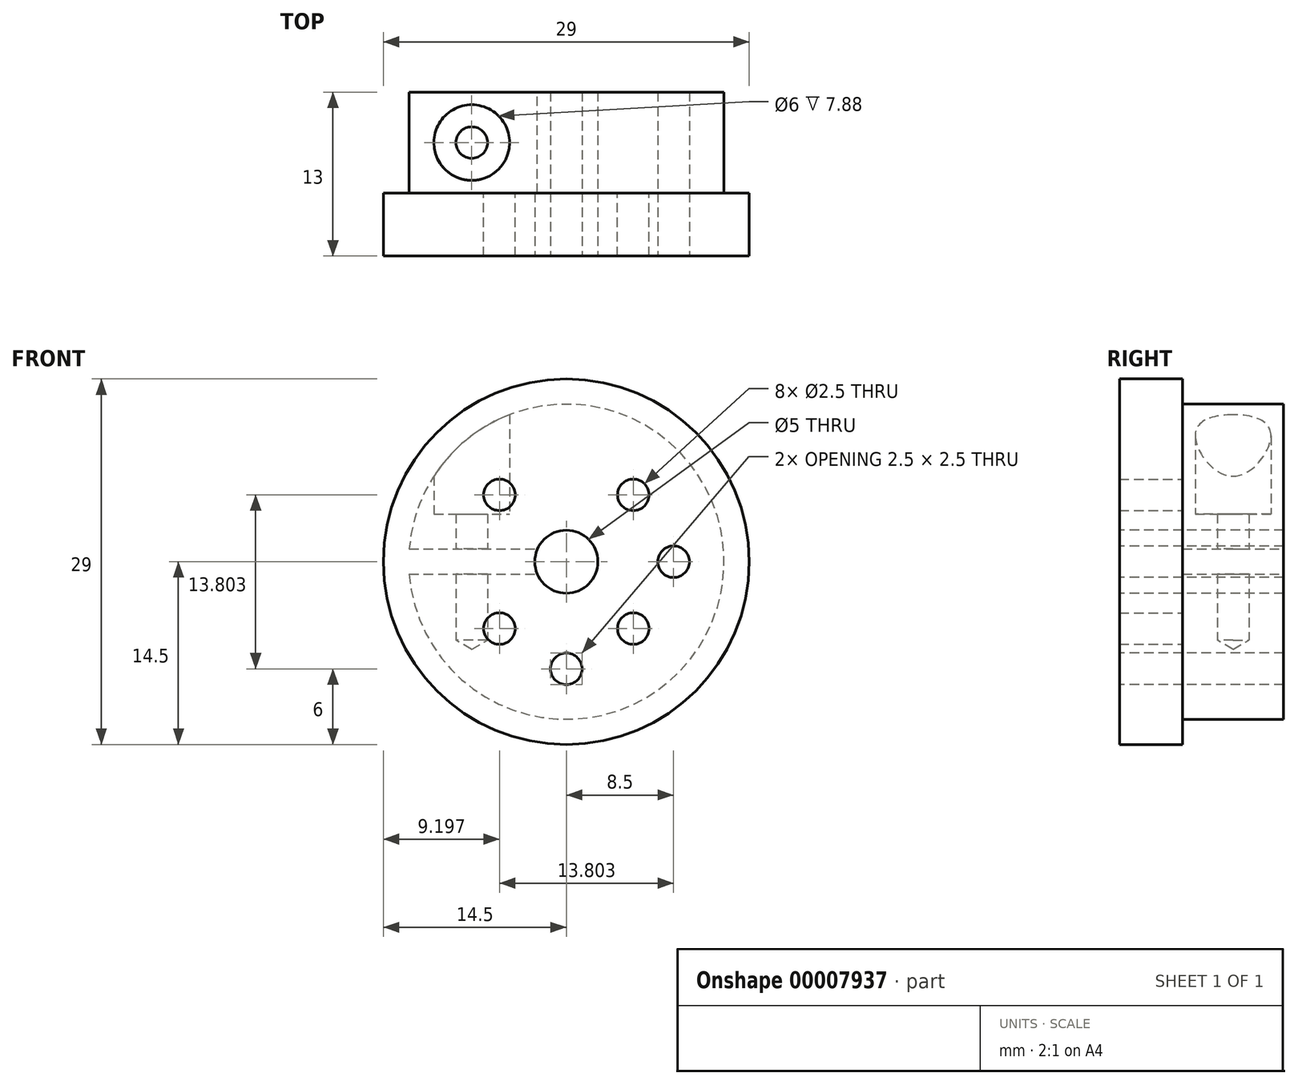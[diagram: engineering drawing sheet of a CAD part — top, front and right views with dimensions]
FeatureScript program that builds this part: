
annotation { "Feature Type Name" : "Feature", "Feature Type Description" : "" }
export const myFeature = defineFeature(function(context is Context, id is Id, definition is map)
    precondition{}
    {
        {
            var Q0;
            Q0=qCreatedBy(makeId("Right.planeOp"),FACE);
            var sketch = newSketch(context, id + "F0", { "sketchPlane" : qUnion([Q0])});
            skLineSegment(sketch, "E0.bottom", {"start": v(-4, 12.5) * mm, "end": v(4, 12.5) * mm});
            skLineSegment(sketch, "E0.top", {"start": v(-4, 2.5) * mm, "end": v(4, 2.5) * mm});
            skLineSegment(sketch, "E0.left", {"start": v(-4, 12.5) * mm, "end": v(-4, 2.5) * mm});
            skLineSegment(sketch, "E0.right", {"start": v(4, 12.5) * mm, "end": v(4, 2.5) * mm});
            skLineSegment(sketch, "E1", {"start": v(-8.98, 0) * mm, "end": v(8.74, 0) * mm, "construction": true});
            skLineSegment(sketch, "E2", {"start": v(0, 0) * mm, "end": v(0, 20.32) * mm, "construction": true});
            skPoint(sketch, "E3", {"position": v(0, 12.5) * mm});
            skLineSegment(sketch, "E4.bottom", {"start": v(-4, 2.5) * mm, "end": v(-9, 2.5) * mm});
            skLineSegment(sketch, "E4.top", {"start": v(-4, 14.5) * mm, "end": v(-9, 14.5) * mm});
            skLineSegment(sketch, "E4.left", {"start": v(-4, 2.5) * mm, "end": v(-4, 14.5) * mm});
            skLineSegment(sketch, "E4.right", {"start": v(-9, 2.5) * mm, "end": v(-9, 14.5) * mm});
            skSolve(sketch);
        }
        {
            var Q0;
            Q0=makeQuery(id+"F0.imprint","IMPRINT",FACE,{"disambiguationData":[TD([[makeQuery(id+"F0.imprint","IMPRINT",EDGE,{"derivedFrom":sQuery(id+"F0.wireOp",EDGE,"E0.bottom")}),-1.0]])]});
            var Q1;
            Q1=sQuery(id+"F0.wireOp",EDGE,"E1");
            revolve(context, id + "F1", {"entities" : qUnion([Q0]), "axis" : qUnion([Q1]), "revolveType" : RevolveType.FULL});
        }
        {
            var Q0;
            Q0=makeQuery(id+"F1.opRevolve","SWEPT_FACE",FACE,{"disambiguationData":[OSD([sQuery(id+"F0.wireOp",EDGE,"E0.right")])]});
            var sketch = newSketch(context, id + "F2", { "sketchPlane" : qUnion([Q0])});
            skPoint(sketch, "E5", {"position": v(-8.5, 0) * mm});
            skPoint(sketch, "E6.1.0", {"position": v(0, -8.5) * mm});
            skPoint(sketch, "E6.center", {"position": v(0, 0) * mm});
            skLineSegment(sketch, "E6.anchor1", {"start": v(0, 0) * mm, "end": v(-8.5, 0) * mm, "construction": true});
            skLineSegment(sketch, "E6.anchor2", {"start": v(0, 0) * mm, "end": v(0, -8.5) * mm, "construction": true});
            skLineSegment(sketch, "E7.bottom", {"start": v(12.73, 1) * mm, "end": v(2.1, 1) * mm});
            skLineSegment(sketch, "E7.top", {"start": v(12.73, -1) * mm, "end": v(2.1, -1) * mm});
            skLineSegment(sketch, "E7.left", {"start": v(12.73, 1) * mm, "end": v(12.73, -1) * mm});
            skLineSegment(sketch, "E7.right", {"start": v(2.1, 1) * mm, "end": v(2.1, -1) * mm});
            skPoint(sketch, "E7.middle", {"position": v(7.42, 0) * mm});
            skSolve(sketch);
        }
        {
            var Q0;
            {var subQ0=sQuery(id+"F2.wireOp",EDGE,"E7.bottom");var subQ1=sQuery(id+"F0.wireOp",EDGE,"E0.right");var subQ2=makeQuery(id+"F1.opRevolve","SWEPT_EDGE",EDGE,{"disambiguationData":[OSD([sQuery(id+"F0.wireOp",EDGE,"E0.bottom"),subQ1])]});var subQ3=makeQuery(id+"F2.imprint","INTERSECT",VERTEX,{"derivedFrom":[subQ2,subQ0]});Q0=makeQuery(id+"F2.imprint","IMPRINT",FACE,{"disambiguationData":[TD([[makeQuery(id+"F2.imprint","IMPRINT",EDGE,{"disambiguationData":[TD([[subQ3,-1.0]])],"derivedFrom":subQ0}),1.0]])]});}
            extrude(context, id + "F3", {"entities" : qUnion([Q0]), "operationType" : NewBodyOperationType.REMOVE, "endBound" : BoundingType.THROUGH_ALL, "oppositeDirection" : true, "depth" : 25 * mm});
        }
        {
            var Q0;
            Q0=qCreatedBy(makeId("Top.planeOp"),FACE);
            cPlane(context, id + "F4", {"entities" : qUnion([Q0]), "cplaneType" : CPlaneType.OFFSET, "offset" : 12.5 * mm, "width" : 150 * mm, "height" : 150 * mm});
        }
        {
            var Q0;
            Q0=qCreatedBy(id+"F4.planeOp",FACE);
            var sketch = newSketch(context, id + "F5", { "sketchPlane" : qUnion([Q0])});
            skLineSegment(sketch, "E8", {"start": v(0, 0) * mm, "end": v(-12.46, 0) * mm, "construction": true});
            skPoint(sketch, "E9", {"position": v(-7.5, 0) * mm});
            skLineSegment(sketch, "E10.0", {"start": v(-12.46, -4) * mm, "end": v(-12.46, 4) * mm});
            skSolve(sketch);
        }
        {
            var Q0;
            Q0=sQuery(id+"F5.wireOp",VERTEX,"E9");
            var Q1;
            Q1=makeQuery(id+"F1.opRevolve","SWEPT_BODY",BODY,{"disambiguationData":[OSD([sQuery(id+"F0.wireOp",EDGE,"E0.bottom"),sQuery(id+"F0.wireOp",EDGE,"E0.top"),sQuery(id+"F0.wireOp",EDGE,"E0.right"),sQuery(id+"F0.wireOp",EDGE,"E4.left")])]});
            hole(context, id + "F6", {"style" : HoleStyle.C_BORE, "endStyle" : HoleEndStyle.BLIND, "holeDiameter" : 2.5 * mm, "cBoreDiameter" : 6 * mm, "cBoreDepth" : 3 * mm, "holeDepth" : 13 * mm, "locations" : qUnion([Q0]), "scope" : qUnion([Q1])});
        }
        {
            var Q0;
            {var subQ3=sQuery(id+"F0.wireOp",EDGE,"E4.bottom");Q0=makeQuery(id+"F0.imprint","IMPRINT",FACE,{"disambiguationData":[TD([[makeQuery(id+"F0.imprint","IMPRINT",EDGE,{"derivedFrom":subQ3}),-1.0]])]});}
            var Q1;
            Q1=sQuery(id+"F0.wireOp",EDGE,"E1");
            revolve(context, id + "F7", {"entities" : qUnion([Q0]), "axis" : qUnion([Q1]), "revolveType" : RevolveType.FULL});
        }
        {
            var Q0;
            Q0=sQuery(id+"F2.wireOp",VERTEX,"E5");
            var Q1;
            Q1=sQuery(id+"F2.wireOp",VERTEX,"E6.1.0");
            var Q2;
            Q2=makeQuery(id+"F1.opRevolve","SWEPT_BODY",BODY,{"disambiguationData":[OSD([sQuery(id+"F0.wireOp",EDGE,"E0.bottom"),sQuery(id+"F0.wireOp",EDGE,"E0.top"),sQuery(id+"F0.wireOp",EDGE,"E0.right"),sQuery(id+"F0.wireOp",EDGE,"E4.left")])]});
            var Q3;
            Q3=makeQuery(id+"F7.opRevolve","SWEPT_BODY",BODY,{"disambiguationData":[OSD([sQuery(id+"F0.wireOp",EDGE,"E4.bottom"),sQuery(id+"F0.wireOp",EDGE,"E4.top"),sQuery(id+"F0.wireOp",EDGE,"E4.left"),sQuery(id+"F0.wireOp",EDGE,"E4.right")])]});
            hole(context, id + "F8", {"style" : HoleStyle.SIMPLE, "endStyle" : HoleEndStyle.THROUGH, "standardTappedOrClearance" : lookupTablePath({ "standard" : "ISO", "engagement" : "75%", "pitch" : "0.5 mm", "size" : "M3", "type" : "Tapped" }), "standardBlindInLast" : lookupTablePath({ "standard" : "ISO", "engagement" : "75%", "pitch" : "0.5 mm", "size" : "M3", "type" : "Tapped" }), "holeDiameter" : 2.5 * mm, "locations" : qUnion([Q0, Q1]), "scope" : qUnion([Q2, Q3]), "isTappedThrough" : true, "majorDiameter" : 3 * mm, "showTappedDepth" : true});
        }
        {
            var Q0;
            Q0=makeQuery(id+"F7.opRevolve","SWEPT_FACE",FACE,{"disambiguationData":[OSD([sQuery(id+"F0.wireOp",EDGE,"E4.right")])]});
            var sketch = newSketch(context, id + "F9", { "sketchPlane" : qUnion([Q0])});
            skPoint(sketch, "E11", {"position": v(-5.3, 5.3) * mm});
            skLineSegment(sketch, "E12", {"start": v(-5.3, 5.3) * mm, "end": v(0, 5.3) * mm, "construction": true});
            skLineSegment(sketch, "E13", {"start": v(-5.3, 5.3) * mm, "end": v(-5.3, 0) * mm, "construction": true});
            skPoint(sketch, "E14.1.0", {"position": v(-5.3, -5.3) * mm});
            skPoint(sketch, "E14.2.0", {"position": v(5.3, -5.3) * mm});
            skPoint(sketch, "E14.3.0", {"position": v(5.3, 5.3) * mm});
            skPoint(sketch, "E14.center", {"position": v(0, 0) * mm});
            skSolve(sketch);
        }
        {
            var Q0;
            Q0=sQuery(id+"F9.wireOp",VERTEX,"E14.2.0");
            var Q1;
            Q1=sQuery(id+"F9.wireOp",VERTEX,"E14.1.0");
            var Q2;
            Q2=sQuery(id+"F9.wireOp",VERTEX,"E11");
            var Q3;
            Q3=sQuery(id+"F9.wireOp",VERTEX,"E14.3.0");
            var Q4;
            Q4=makeQuery(id+"F7.opRevolve","SWEPT_BODY",BODY,{"disambiguationData":[OSD([sQuery(id+"F0.wireOp",EDGE,"E4.bottom"),sQuery(id+"F0.wireOp",EDGE,"E4.top"),sQuery(id+"F0.wireOp",EDGE,"E4.left"),sQuery(id+"F0.wireOp",EDGE,"E4.right")])]});
            hole(context, id + "F10", {"style" : HoleStyle.SIMPLE, "endStyle" : HoleEndStyle.THROUGH, "standardTappedOrClearance" : lookupTablePath({ "standard" : "ISO", "fit" : "Normal", "engagement" : "75%", "pitch" : "0.5 mm", "size" : "M3", "type" : "Tapped" }), "standardBlindInLast" : lookupTablePath({ "fit" : "Standard", "standard" : "ISO", "engagement" : "75%", "pitch" : "0.5 mm", "size" : "M3", "type" : "Tapped" }), "holeDiameter" : 2.5 * mm, "locations" : qUnion([Q0, Q1, Q2, Q3]), "scope" : qUnion([Q4]), "isTappedThrough" : true, "majorDiameter" : 3 * mm, "showTappedDepth" : true});
        }
    });
